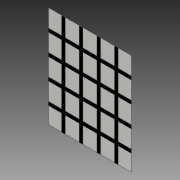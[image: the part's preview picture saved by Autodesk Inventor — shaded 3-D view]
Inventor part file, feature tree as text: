
AUTODESK INVENTOR PART (.ipt)
format: ipt  version: 2016 SP1 (Build 200210100, 210)  size: 374,272 bytes
history: native  units: in
note: dims shown in document units (in); Inventor stores cm internally (conversion verified against a paired STEP export)
features: extrude x1, sketch x1, projected_geometry x1, imported_body x1
ambient origin geometry x8: Origin, YZ Plane, XZ Plane, XY Plane, X Axis, Y Axis, Z Axis, Center Point
bodies: Solid1 (feature_tree), Solid2 (feature_tree)
feature tree (4):
  extrude  "Extrusion1"  [1 undecoded]
  sketch  "Sketch1"  dims[d0=0.2in d1=0.0in]
  projected_geometry  "Projected Loop1"
  imported_body  "Base1"
note: 1 required parameter value undecoded (feature->parameter linkage not recoverable at this tier; creation-order binding heuristic only, values carry confidence <= 0.55)
